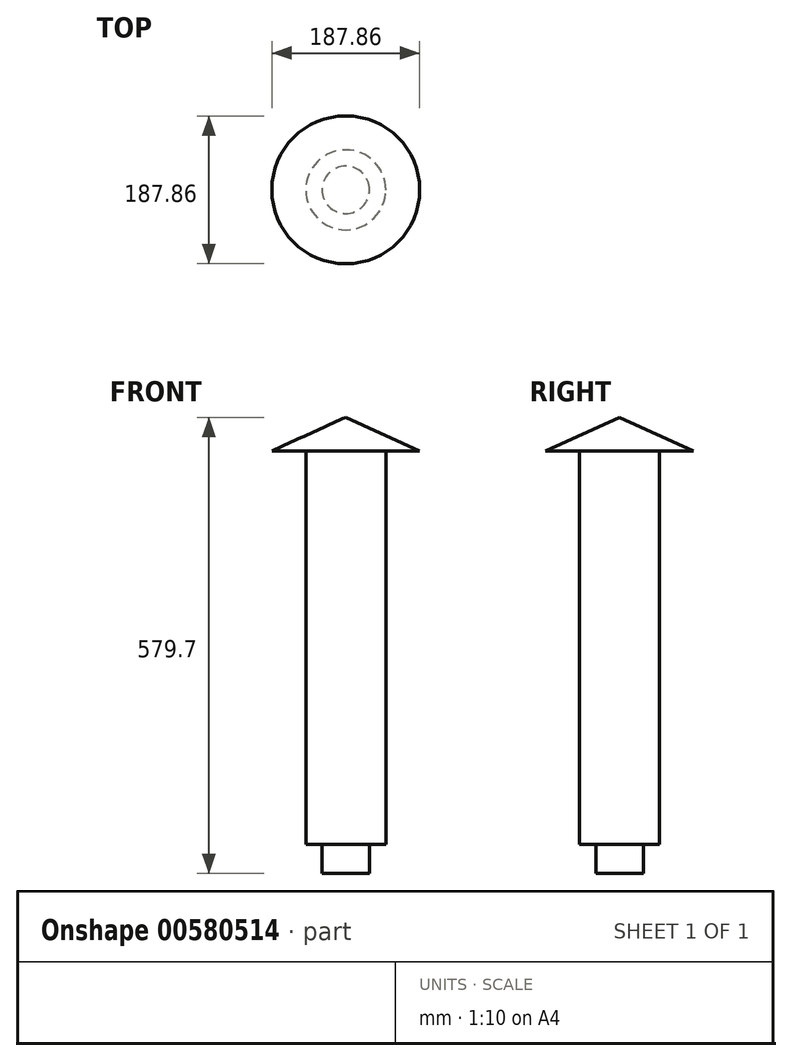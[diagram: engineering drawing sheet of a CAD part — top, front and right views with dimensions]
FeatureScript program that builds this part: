
annotation { "Feature Type Name" : "Feature", "Feature Type Description" : "" }
export const myFeature = defineFeature(function(context is Context, id is Id, definition is map)
    precondition{}
    {
        {
            var Q0;
            Q0=qCreatedBy(makeId("Top.planeOp"),FACE);
            var sketch = newSketch(context, id + "F0", { "sketchPlane" : qUnion([Q0])});
            skCircle(sketch, "E0", {"center": v(0, 0) * mm, "radius": 50.78 * mm});
            skSolve(sketch);
        }
        {
            var Q0;
            Q0 = qSketchRegion(id + "F0", true);
            extrude(context, id + "F1", {"entities" : qUnion([Q0]), "depth" : 500 * mm, "offsetDistance" : 25 * mm});
        }
        {
            var Q0;
            Q0=qCreatedBy(makeId("Front.planeOp"),FACE);
            var sketch = newSketch(context, id + "F2", { "sketchPlane" : qUnion([Q0])});
            skLineSegment(sketch, "E1", {"start": v(0, 542.7) * mm, "end": v(0, 500) * mm});
            skLineSegment(sketch, "E2", {"start": v(0, 500) * mm, "end": v(93.93, 500) * mm});
            skLineSegment(sketch, "E3", {"start": v(0, 542.7) * mm, "end": v(93.93, 500) * mm});
            skSolve(sketch);
        }
        {
            var Q0;
            Q0=makeQuery(id+"F2.imprint","IMPRINT",FACE,{"disambiguationData":[TD([[makeQuery(id+"F2.imprint","IMPRINT",EDGE,{"derivedFrom":sQuery(id+"F2.wireOp",EDGE,"E1")}),1.0]])]});
            var Q1;
            Q1=sQuery(id+"F2.wireOp",EDGE,"E1");
            revolve(context, id + "F3", {"operationType" : NewBodyOperationType.ADD, "entities" : qUnion([Q0]), "axis" : qUnion([Q1]), "revolveType" : RevolveType.FULL});
        }
        {
            var Q0;
            Q0=makeQuery(id+"F1.opExtrude","CAP_FACE",FACE,{"disambiguationData":[OSD([sQuery(id+"F0.wireOp",EDGE,"E0")])],"isStart":true});
            var sketch = newSketch(context, id + "F4", { "sketchPlane" : qUnion([Q0])});
            skCircle(sketch, "E4", {"center": v(0, 0) * mm, "radius": 30.05 * mm});
            skSolve(sketch);
        }
        {
            var Q0;
            Q0 = qSketchRegion(id + "F4", true);
            extrude(context, id + "F5", {"entities" : qUnion([Q0]), "operationType" : NewBodyOperationType.ADD, "depth" : 37 * mm, "offsetDistance" : 25 * mm});
        }
    });
